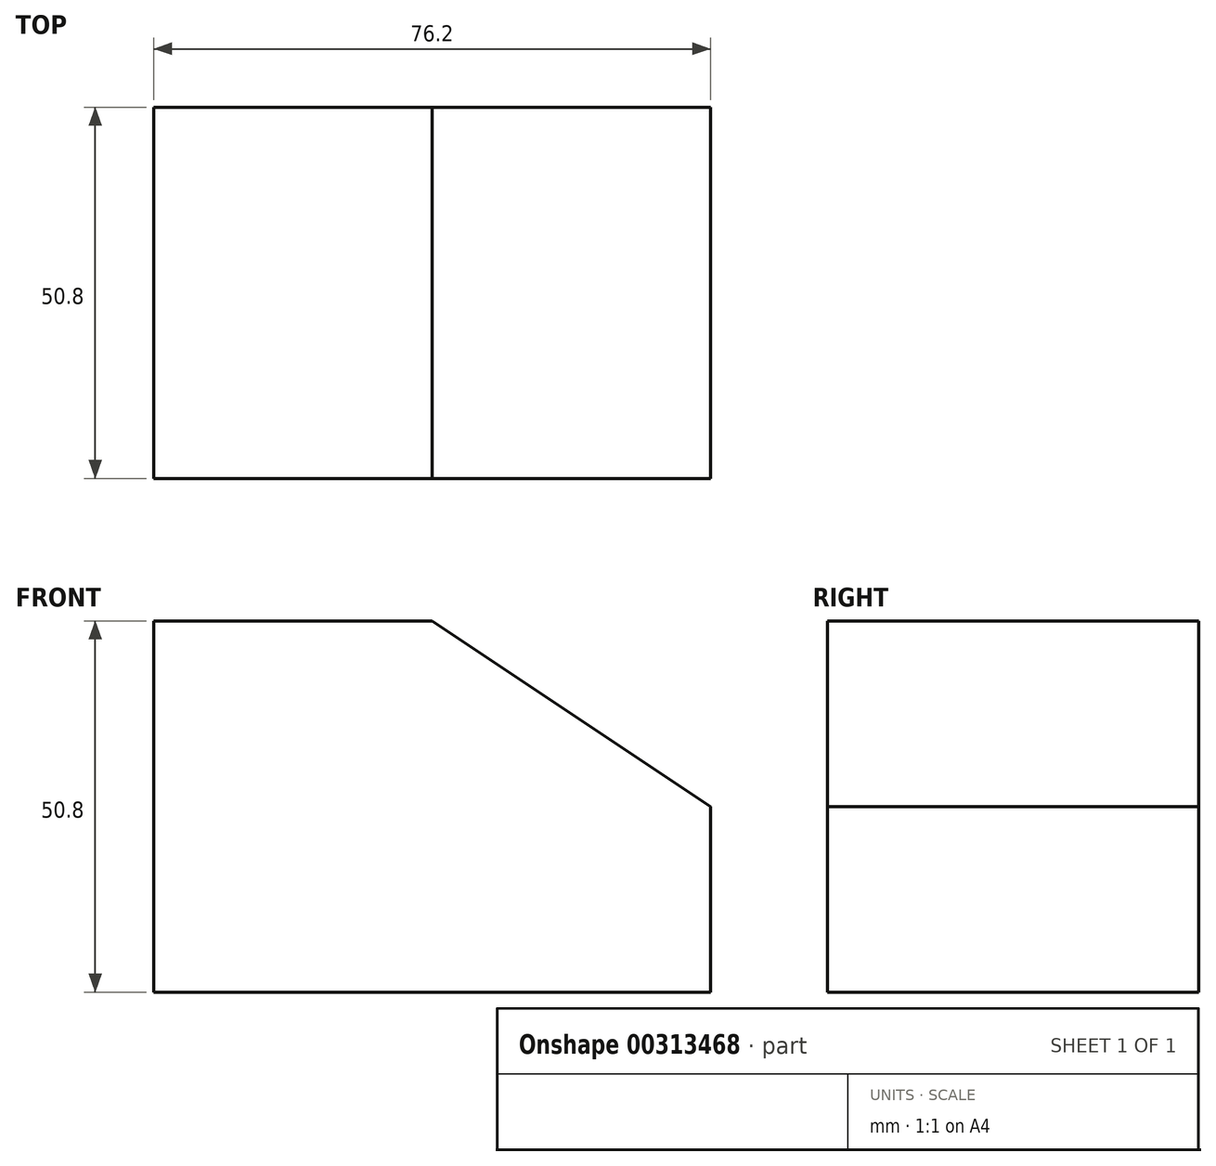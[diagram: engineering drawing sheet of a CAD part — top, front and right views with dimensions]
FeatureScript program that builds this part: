
annotation { "Feature Type Name" : "Feature", "Feature Type Description" : "" }
export const myFeature = defineFeature(function(context is Context, id is Id, definition is map)
    precondition{}
    {
        {
            var Q0;
            Q0=qCreatedBy(makeId("Front.planeOp"),FACE);
            var sketch = newSketch(context, id + "F0", { "sketchPlane" : qUnion([Q0])});
            skLineSegment(sketch, "E0", {"start": v(-35.62, -40.03) * mm, "end": v(40.58, -40.03) * mm});
            skLineSegment(sketch, "E1", {"start": v(40.58, -40.03) * mm, "end": v(40.58, -14.63) * mm});
            skLineSegment(sketch, "E2", {"start": v(40.58, -14.63) * mm, "end": v(2.48, 10.77) * mm});
            skLineSegment(sketch, "E3", {"start": v(2.48, 10.77) * mm, "end": v(-35.62, 10.77) * mm});
            skLineSegment(sketch, "E4", {"start": v(-35.62, 10.77) * mm, "end": v(-35.62, -40.03) * mm});
            skSolve(sketch);
        }
        {
            var Q0;
            Q0=makeQuery(id+"F0.imprint","IMPRINT",FACE,{"disambiguationData":[TD([[makeQuery(id+"F0.imprint","IMPRINT",EDGE,{"derivedFrom":sQuery(id+"F0.wireOp",EDGE,"E0")}),1.0]])]});
            extrude(context, id + "F1", {"entities" : qUnion([Q0]), "depth" : 50.8 * mm});
        }
    });
